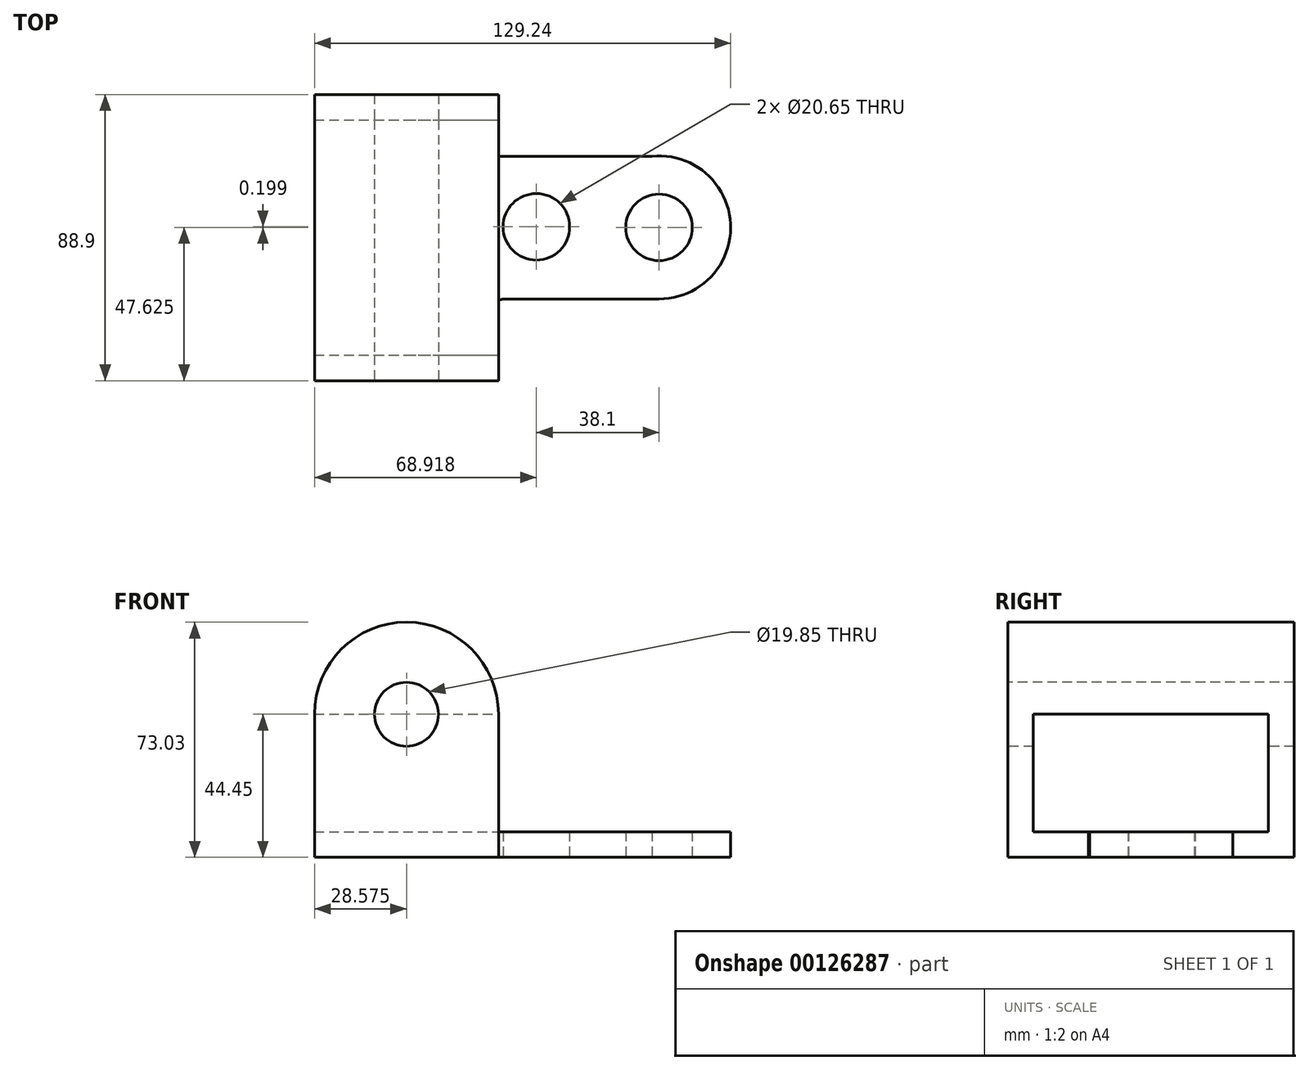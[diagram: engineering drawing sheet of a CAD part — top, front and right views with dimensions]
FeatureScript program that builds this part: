
annotation { "Feature Type Name" : "Feature", "Feature Type Description" : "" }
export const myFeature = defineFeature(function(context is Context, id is Id, definition is map)
    precondition{}
    {
        {
            var Q0;
            Q0=qCreatedBy(makeId("Front.planeOp"),FACE);
            var sketch = newSketch(context, id + "F0", { "sketchPlane" : qUnion([Q0])});
            skLineSegment(sketch, "E0", {"start": v(0, 0) * mm, "end": v(0, 44.45) * mm});
            skArc(sketch, "E1", {"start": v(57.15, 44.45) * mm, "mid": v(28.57, 73.03) * mm, "end": v(0, 44.45) * mm});
            skLineSegment(sketch, "E2", {"start": v(57.15, 44.45) * mm, "end": v(57.15, 0) * mm});
            skCircle(sketch, "E3", {"center": v(28.58, 44.45) * mm, "radius": 9.92 * mm});
            skLineSegment(sketch, "E4", {"start": v(57.15, 7.94) * mm, "end": v(0, 7.94) * mm, "construction": true});
            skLineSegment(sketch, "E5", {"start": v(28.57, 58.82) * mm, "end": v(28.58, 29.8) * mm, "construction": true});
            skLineSegment(sketch, "E6", {"start": v(13.74, 44.45) * mm, "end": v(43.54, 44.45) * mm, "construction": true});
            skLineSegment(sketch, "E7", {"start": v(0, 0) * mm, "end": v(57.15, 0) * mm});
            skSolve(sketch);
        }
        {
            var Q0;
            Q0=qCreatedBy(makeId("Top.planeOp"),FACE);
            var sketch = newSketch(context, id + "F1", { "sketchPlane" : qUnion([Q0])});
            skLineSegment(sketch, "E8", {"start": v(53.04, 0) * mm, "end": v(53.04, 19.05) * mm});
            skLineSegment(sketch, "E9", {"start": v(50.8, 88.9) * mm, "end": v(0, 88.9) * mm});
            skLineSegment(sketch, "E10", {"start": v(53.04, 0) * mm, "end": v(0, 0) * mm});
            skLineSegment(sketch, "E11", {"start": v(0, 0) * mm, "end": v(0, 88.9) * mm});
            skLineSegment(sketch, "E12", {"start": v(50.8, 88.9) * mm, "end": v(50.8, 76.09) * mm});
            skArc(sketch, "E13", {"start": v(50.8, 76.09) * mm, "mid": v(52.66, 71.6) * mm, "end": v(57.15, 69.74) * mm});
            skArc(sketch, "E14", {"start": v(59.4, 25.4) * mm, "mid": v(54.9, 23.54) * mm, "end": v(53.04, 19.05) * mm});
            skLineSegment(sketch, "E15", {"start": v(59.4, 25.4) * mm, "end": v(107.02, 25.4) * mm});
            skLineSegment(sketch, "E16", {"start": v(57.15, 69.74) * mm, "end": v(104.77, 69.74) * mm});
            skArc(sketch, "E17", {"start": v(107.02, 25.4) * mm, "mid": v(129.21, 48.75) * mm, "end": v(104.77, 69.74) * mm});
            skCircle(sketch, "E18", {"center": v(107.02, 47.62) * mm, "radius": 10.33 * mm});
            skCircle(sketch, "E19", {"center": v(68.92, 47.82) * mm, "radius": 10.33 * mm});
            skLineSegment(sketch, "E20", {"start": v(0, 10.27) * mm, "end": v(53.04, 10.27) * mm});
            skLineSegment(sketch, "E21", {"start": v(0, 81.9) * mm, "end": v(50.8, 81.9) * mm});
            skSolve(sketch);
        }
        {
            var Q0;
            Q0 = qSketchRegion(id + "F1", true);
            extrude(context, id + "F2", {"entities" : qUnion([Q0]), "depth" : 7.94 * mm});
        }
        {
            var Q0;
            Q0 = qSketchRegion(id + "F0", true);
            extrude(context, id + "F3", {"entities" : qUnion([Q0]), "operationType" : NewBodyOperationType.ADD, "oppositeDirection" : true, "depth" : 88.9 * mm});
        }
        {
            var Q0;
            Q0=makeQuery(id+"F3.opExtrude","SWEPT_FACE",FACE,{"disambiguationData":[OSD([sQuery(id+"F0.wireOp",EDGE,"E2")])]});
            var sketch = newSketch(context, id + "F4", { "sketchPlane" : qUnion([Q0])});
            skLineSegment(sketch, "E22.bottom", {"start": v(7.94, 44.45) * mm, "end": v(80.96, 44.45) * mm});
            skLineSegment(sketch, "E22.top", {"start": v(7.94, 7.94) * mm, "end": v(80.96, 7.94) * mm});
            skLineSegment(sketch, "E22.left", {"start": v(7.94, 44.45) * mm, "end": v(7.94, 7.94) * mm});
            skLineSegment(sketch, "E22.right", {"start": v(80.96, 44.45) * mm, "end": v(80.96, 7.94) * mm});
            skSolve(sketch);
        }
        {
            var Q0;
            Q0 = qSketchRegion(id + "F4", true);
            extrude(context, id + "F5", {"entities" : qUnion([Q0]), "operationType" : NewBodyOperationType.REMOVE, "endBound" : BoundingType.UP_TO_NEXT, "oppositeDirection" : true, "depth" : 25.4 * mm});
        }
    });
